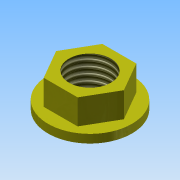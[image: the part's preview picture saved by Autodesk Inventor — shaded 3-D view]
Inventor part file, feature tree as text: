
AUTODESK INVENTOR PART (.ipt)
format: ipt  version: 2015 (Build 190159000, 159)  size: 100,352 bytes
history: native  units: mm
features: extrude x3, sketch x3, thread x1
ambient origin geometry x8: Origin, YZ Plane, XZ Plane, XY Plane, X Axis, Y Axis, Z Axis, Center Point
bodies: 实体1 (feature_tree)
feature tree (7):
  extrude  "拉伸1"  Depth=2.0mm TaperAngle=0.0deg
  extrude  "拉伸2"  Depth=6.0mm TaperAngle=0.0deg
  extrude  "拉伸3"  Depth=6.0mm TaperAngle=0.0deg
  thread  "螺纹1"  [1 undecoded]
  sketch  "草图1"  dims[d0=20.0mm d1=2.0mm d2=0.0mm]
  sketch  "草图2"  dims[d3=14.0mm d4=6.0mm d5=0.0mm]
  sketch  "草图3"  dims[d6=10.0mm d7=6.0mm d8=0.0mm d9=10.0mm d10=0.0mm]
note: 1 required parameter value undecoded (feature->parameter linkage not recoverable at this tier; creation-order binding heuristic only, values carry confidence <= 0.55)
